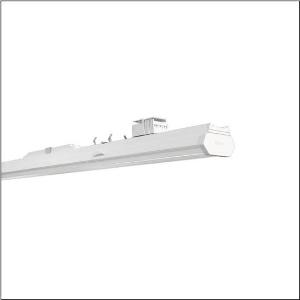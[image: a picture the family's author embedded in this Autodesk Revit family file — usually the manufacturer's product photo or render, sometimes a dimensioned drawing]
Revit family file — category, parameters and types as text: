
# Revit family: licross_r__11_protected_mo_51td1bdn49xg_f089
name_source: partatom
category: Lighting Fixtures
units: mm (PartAtom-declared; Revit-internal decimal feet)

## family parameters
Cut with Voids When Loaded = No
Host = Face
Light Source = No
Part Type = Normal
Room Calculation Point = No
Round Connector Dimension = Use Diameter
Shared = No

## types (1)
- --- (1 x LED, 9370 lm, 57.1 W, 4000K)
    Apparent Load = 57 VA
    CIE Flux Codes = 54 82 95 97 100
    Color Rendering = 80
    Color Temperature = 4000K
    Default Elevation = 1800 mm
    Description = Licross® 11 Protected MO, luminaire insert, of sheet steel, galvanised, coil coated, white, length: 1.500mm, width: 90mm, height: 101mm, LED rated luminous flux: 9.370lm, light colour: 840, control gear: DALI 2, with plug, 5-pole, with phase selection, mains connection: 220..240V, AC, 50/60Hz, rated input power: 57W, halogen-free wiring, primary optical cover: cover, of PMMA, light emission: direct distribution, primary light characteristic: symmetric, protection rating (complete): IP54, insulation class (complete): insulation class I (protective earthing), certification: CE, ENEC, VDE, UKCA, protection symbol: D if used in an environment with non-conductive dust loads with corresponding accessories, impact resistance: IK06, permissible ambient temperature for indoor applications: -25..+35°C, corresponds to IFS (International Featured Standards) requirements for safety and quality in the food industry, reducing of maximum allowable ambient temperature of 5°C with ceiling mounting, LABS conformity tested according to VDMA 24364:2018-05, packaging unit: 1 piece
    Height = 92 mm
    Lamp = 1 x LED
    Lamp Light Flux = 9370 lm
    Lamp Power = 57.1 W
    Lamp count = 1
    Length = 1500 mm
    Luminous efficacy = 164 lm/W
    Manufacturer = Siteco
    ModVariant = No
    Model = 51TD1BDN49XG
    Mounting Place = Ceiling
    Mounting Type = Pendant
    Number of Poles = 1
    OnlyDefault = Yes
    Power Factor = 1
    Product Name = Licross® 11 Protected MO
    Product group = luminaire insert
    ProductGroupID = 901
    Protection Class = Protection class I
    Protection Degree = IP 54
    RLX_Detail_Level = 1
    RLX_Emergency_Light_Flux = 0 lm
    RLX_Emergency_Type = 0
    RLX_Emergency_Type_DB = No
    RlxData = <blob elided: 24373 chars, md5=fbb587b2>
    Socket = socket
    Standby Power = 0 W
    System Light Flux = 9370 lm
    System Power = 57 W
    Type Comments = factory setting: luminous flux: 100 % | dim-lin: 254 | 378 mA
    Type Image = l_1256145.jpg
    URL = http://relux.com
    VarID = @adj_070113
    Voltage = 0 V
    Weight = 0.00 kg
    Width = 88 mm

## geometry (parser evidence)
native form markers: Blend x4, Sweep x11
no freeform markers — native parametric forms only
